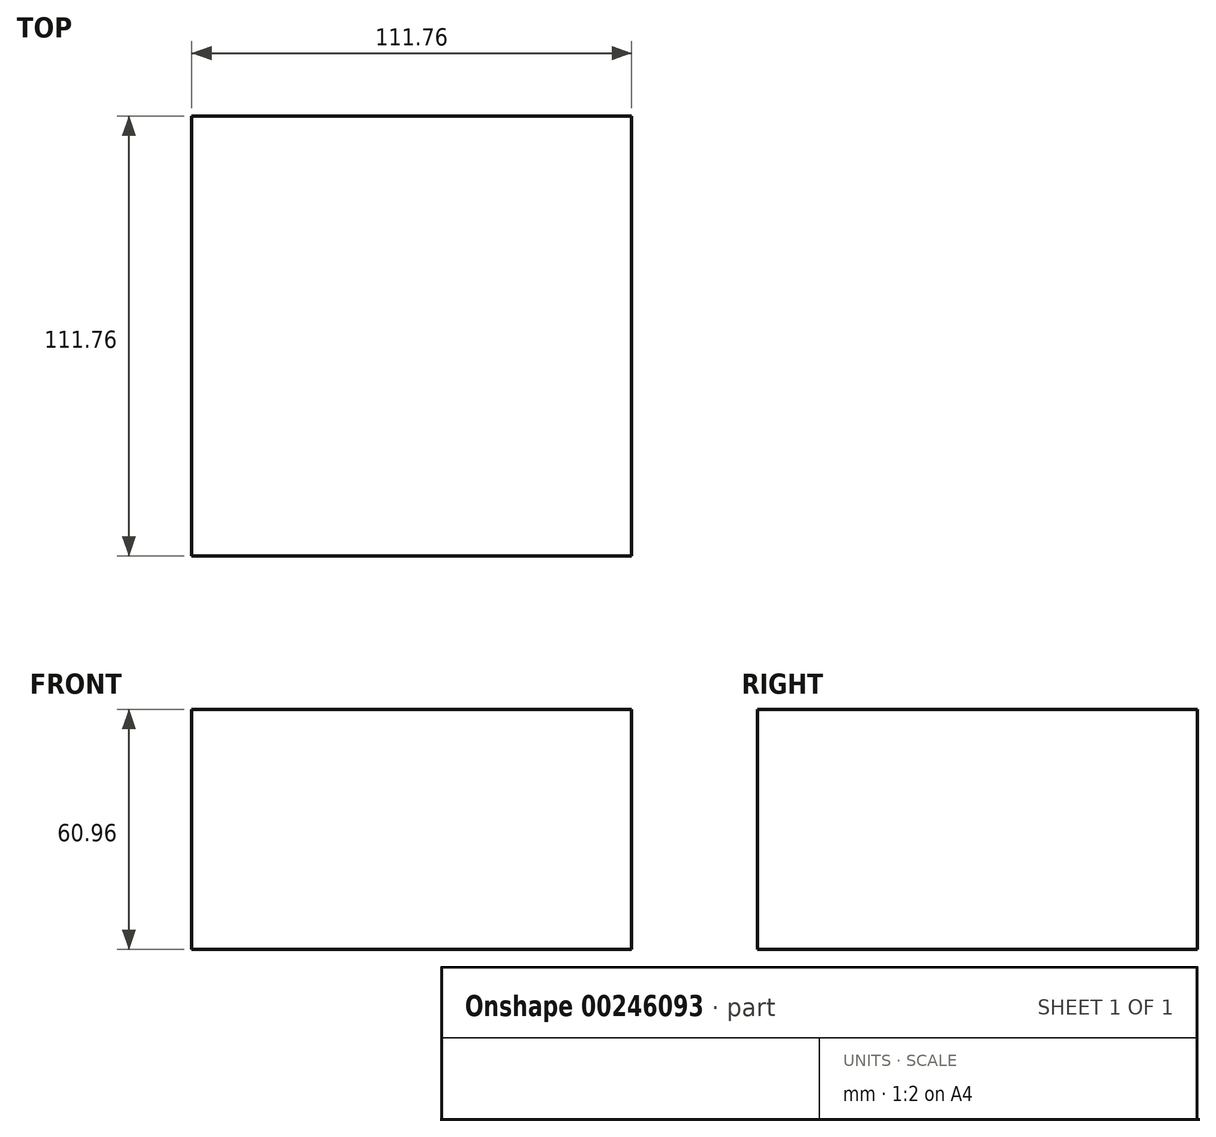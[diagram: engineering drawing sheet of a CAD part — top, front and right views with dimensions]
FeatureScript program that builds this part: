
annotation { "Feature Type Name" : "Feature", "Feature Type Description" : "" }
export const myFeature = defineFeature(function(context is Context, id is Id, definition is map)
    precondition{}
    {
        {
            var Q0;
            Q0=qCreatedBy(makeId("Front.planeOp"),FACE);
            var sketch = newSketch(context, id + "F0", { "sketchPlane" : qUnion([Q0])});
            skLineSegment(sketch, "E0", {"start": v(0, 0) * mm, "end": v(-55.88, 0) * mm});
            skLineSegment(sketch, "E1", {"start": v(-55.88, 0) * mm, "end": v(-55.88, 60.96) * mm});
            skLineSegment(sketch, "E2", {"start": v(-55.88, 60.96) * mm, "end": v(0, 60.96) * mm});
            skLineSegment(sketch, "E3", {"start": v(0, 60.96) * mm, "end": v(55.88, 60.96) * mm});
            skLineSegment(sketch, "E4", {"start": v(55.88, 60.96) * mm, "end": v(55.88, 0) * mm});
            skLineSegment(sketch, "E5", {"start": v(55.88, 0) * mm, "end": v(0, 0) * mm});
            skSolve(sketch);
        }
        {
            var Q0;
            Q0 = qSketchRegion(id + "F0", true);
            extrude(context, id + "F1", {"entities" : qUnion([Q0]), "depth" : 111.76 * mm});
        }
    });
